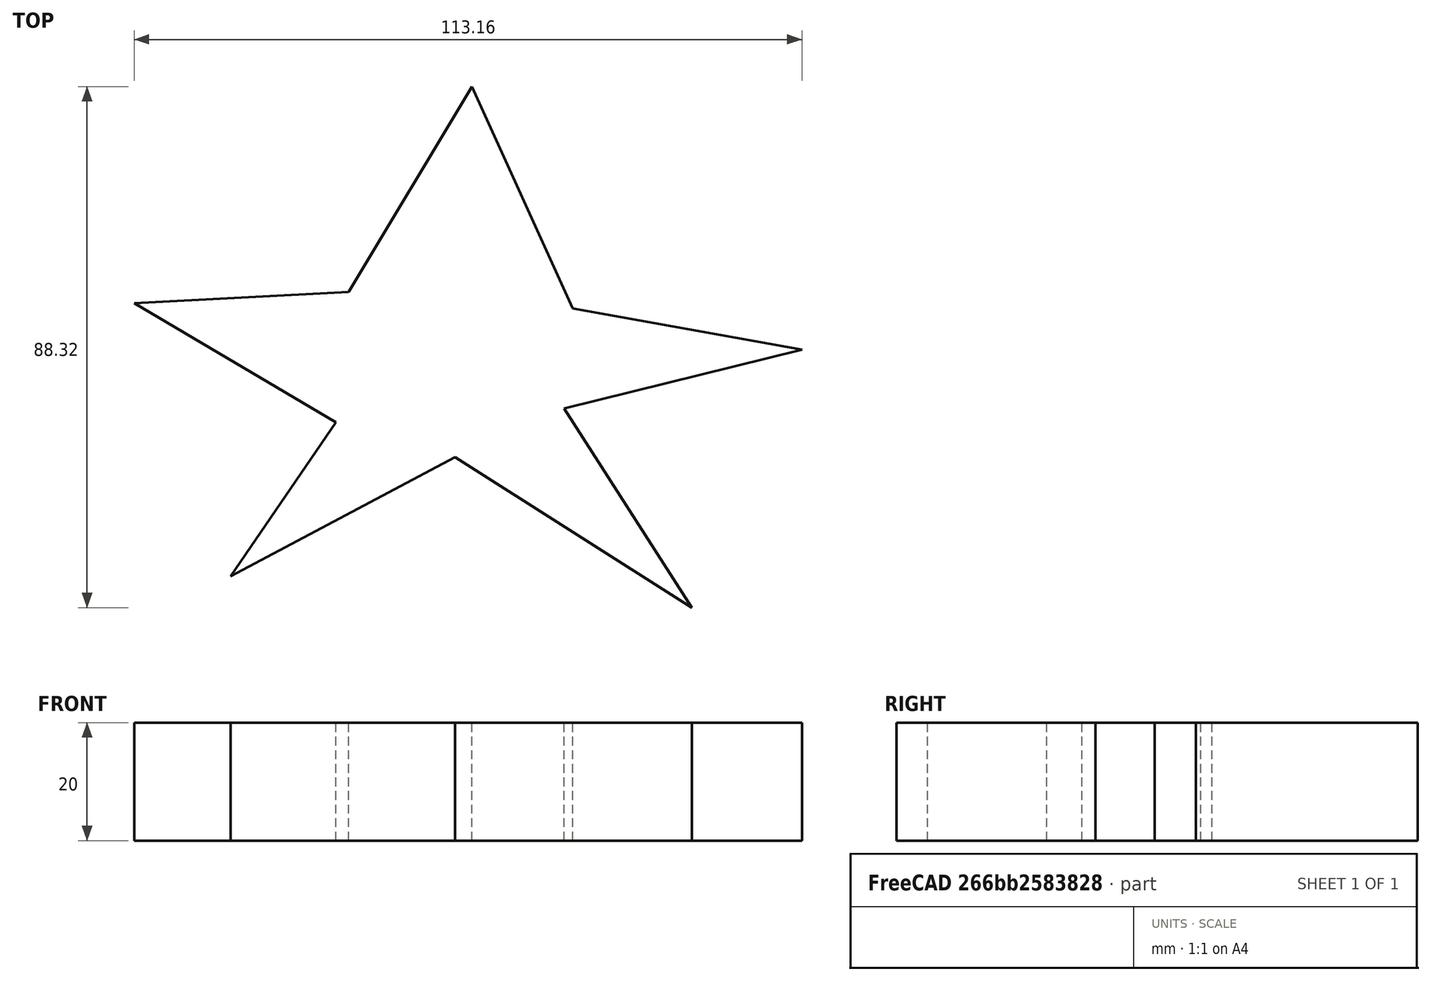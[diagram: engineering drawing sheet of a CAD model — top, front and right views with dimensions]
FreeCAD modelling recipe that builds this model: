
FCSTD DOCUMENT  (FreeCAD 1.0R39319 (Git))
Label: ojt1_t16p01_sketch_star
License: All rights reserved
LicenseURL: https://en.wikipedia.org/wiki/All_rights_reserved
objects: Sketcher::SketchObject×1, PartDesign::Pad×1, PartDesign::Body×1
note: 6 computed .brp shape members not serialized (recipe doc carries the construction recipe); baked Part::Feature solids carry a one-line shape summary decoded from their .brp

FEATURE [Sketcher::SketchObject] Sketch
  ArcFitTolerance = 1e-06
  AttachmentSupport = -> [XY_Plane]
  FullyConstrained = false
  MakeInternals = false
  MapMode = 5
  sketch-geometry (10):
    g0: LineSegment StartX=0 StartY=47.24 StartZ=0 EndX=17.0913 EndY=9.66038 EndZ=0
    g1: LineSegment StartX=17.0913 StartY=9.66038 StartZ=0 EndX=55.9448 EndY=2.65401 EndZ=0
    g2: LineSegment StartX=55.9448 StartY=2.65401 StartZ=0 EndX=15.6051 EndY=-7.32476 EndZ=0
    g3: LineSegment StartX=15.6051 StartY=-7.32476 StartZ=0 EndX=37.2611 EndY=-41.0827 EndZ=0
    g4: LineSegment StartX=37.2611 StartY=-41.0827 StartZ=0 EndX=-2.86627 EndY=-15.605 EndZ=0
    g5: LineSegment StartX=-2.86627 StartY=-15.605 StartZ=0 EndX=-40.8705 EndY=-35.7749 EndZ=0
    g6: LineSegment StartX=-40.8705 StartY=-35.7749 StartZ=0 EndX=-23.0361 EndY=-9.66021 EndZ=0
    g7: LineSegment StartX=-23.0361 StartY=-9.66021 StartZ=0 EndX=-57.2187 EndY=10.5096 EndZ=0
    g8: LineSegment StartX=-57.2187 StartY=10.5096 StartZ=0 EndX=-20.913 EndY=12.4205 EndZ=0
    g9: LineSegment StartX=-20.913 StartY=12.4205 StartZ=0 EndX=0 EndY=47.24 EndZ=0
  constraints (11):
    c: PointOnObject(g0,g-2)
    c: Coincident(g0,g1)
    c: Coincident(g1,g2)
    c: Coincident(g2,g3)
    c: Coincident(g3,g4)
    c: Coincident(g4,g5)
    c: Coincident(g5,g6)
    c: Coincident(g6,g7)
    c: Coincident(g7,g8)
    c: Coincident(g8,g9)
    c: Coincident(g9,g0)
FEATURE [PartDesign::Pad] Pad
  Direction = (0,0,1)
  Length = 20
  Length2 = 10
  Profile = -> Sketch
  ReferenceAxis = -> Sketch [N_Axis]
  Refine = true
  Suppressed = false
  Type = 0
FEATURE [PartDesign::Body] Body
  AllowCompound = false
  Group = -> [Sketch,Pad]
  Origin = -> Origin
  Tip = -> Pad
